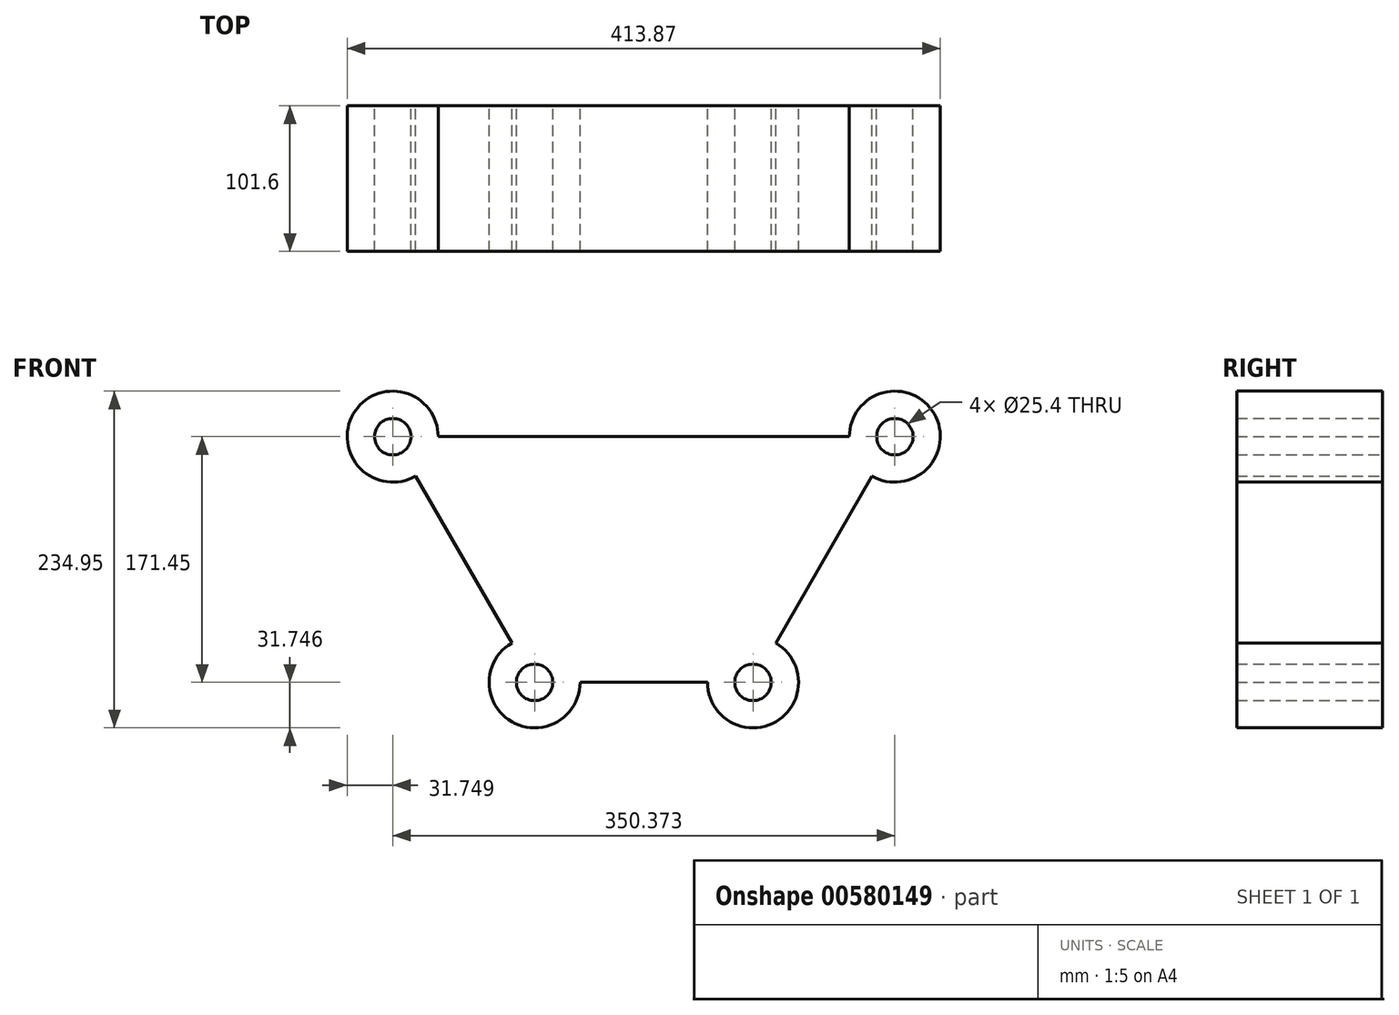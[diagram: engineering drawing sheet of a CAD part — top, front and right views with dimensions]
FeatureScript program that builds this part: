
annotation { "Feature Type Name" : "Feature", "Feature Type Description" : "" }
export const myFeature = defineFeature(function(context is Context, id is Id, definition is map)
    precondition{}
    {
        {
            var Q0;
            Q0=qCreatedBy(makeId("Front.planeOp"),FACE);
            var sketch = newSketch(context, id + "F0", { "sketchPlane" : qUnion([Q0])});
            skLineSegment(sketch, "E0", {"start": v(-73.6, -83.5) * mm, "end": v(78.8, -83.5) * mm});
            skLineSegment(sketch, "E1", {"start": v(78.8, -83.5) * mm, "end": v(177.78, 87.96) * mm});
            skLineSegment(sketch, "E2", {"start": v(177.78, 87.96) * mm, "end": v(-172.6, 87.96) * mm});
            skLineSegment(sketch, "E3", {"start": v(-172.6, 87.96) * mm, "end": v(-73.6, -83.5) * mm});
            skCircle(sketch, "E4", {"center": v(177.78, 87.96) * mm, "radius": 31.75 * mm});
            skCircle(sketch, "E5", {"center": v(177.78, 87.96) * mm, "radius": 12.7 * mm});
            skCircle(sketch, "E6", {"center": v(-172.6, 87.96) * mm, "radius": 12.7 * mm});
            skCircle(sketch, "E7", {"center": v(-172.6, 87.96) * mm, "radius": 31.75 * mm});
            skCircle(sketch, "E8", {"center": v(78.8, -83.5) * mm, "radius": 12.7 * mm});
            skCircle(sketch, "E9", {"center": v(-73.6, -83.5) * mm, "radius": 12.7 * mm});
            skCircle(sketch, "E10", {"center": v(-73.6, -83.5) * mm, "radius": 31.75 * mm});
            skCircle(sketch, "E11", {"center": v(78.8, -83.5) * mm, "radius": 31.75 * mm});
            skSolve(sketch);
        }
        {
            var Q0;
            Q0 = qSketchRegion(id + "F0", true);
            extrude(context, id + "F1", {"entities" : qUnion([Q0]), "endBound" : BoundingType.SYMMETRIC, "depth" : 101.6 * mm, "offsetDistance" : 25.4 * mm});
        }
    });
